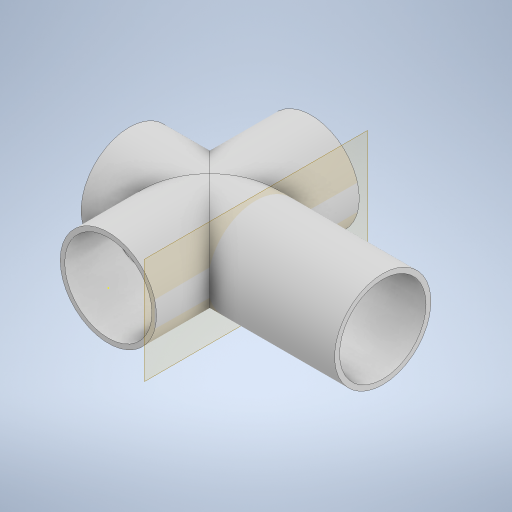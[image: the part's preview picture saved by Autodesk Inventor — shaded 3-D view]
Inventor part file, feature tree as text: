
AUTODESK INVENTOR PART (.ipt)
format: ipt  version: 2024 (Build 280153000, 153)  size: 315,392 bytes
history: native  units: mm
features: sketch x10, extrude x5, other x1, plane x1
ambient origin geometry x8: Origin, YZ Plane, XZ Plane, XY Plane, X Axis, Y Axis, Z Axis, Center Point
bodies: Body1 (feature_tree)
feature tree (17):
  other  "Sólido1"
  extrude  "Extrusión1"  Depth=400.0mm TaperAngle=0.0deg
  sketch  "Boceto2"  dims[d7=190.0mm d8=500.0mm d9=0.0mm]
  sketch  "Boceto 3D1"  dims[d0=190.0mm d1=400.0mm d2=0.0mm]
  sketch  "Boceto 3D2"  dims[d10=500.0mm d11=0.0mm d12=500.0mm d13=0.0mm]
  sketch  "Boceto 3D3"  dims[d14=0.5mm d15=0.872665mm]
  extrude  "Extrusión2"  Depth=400.0mm
  sketch  "Boceto 3D4"
  plane  "Plano de trabajo2"
  extrude  "Extrusión3"  Depth=500.0mm TaperAngle=0.0deg
  extrude  "Extrusión4"  Depth=500.0mm TaperAngle=0.0deg
  extrude  "Extrusión5"  Depth=0.872665mm
  sketch  "Boceto1"  dims[d3=400.0mm d4=0.0mm d6=91.25mm]
  sketch  "Boceto3"
  sketch  "Boceto4"
  sketch  "Boceto5"
  sketch  "Boceto6"
